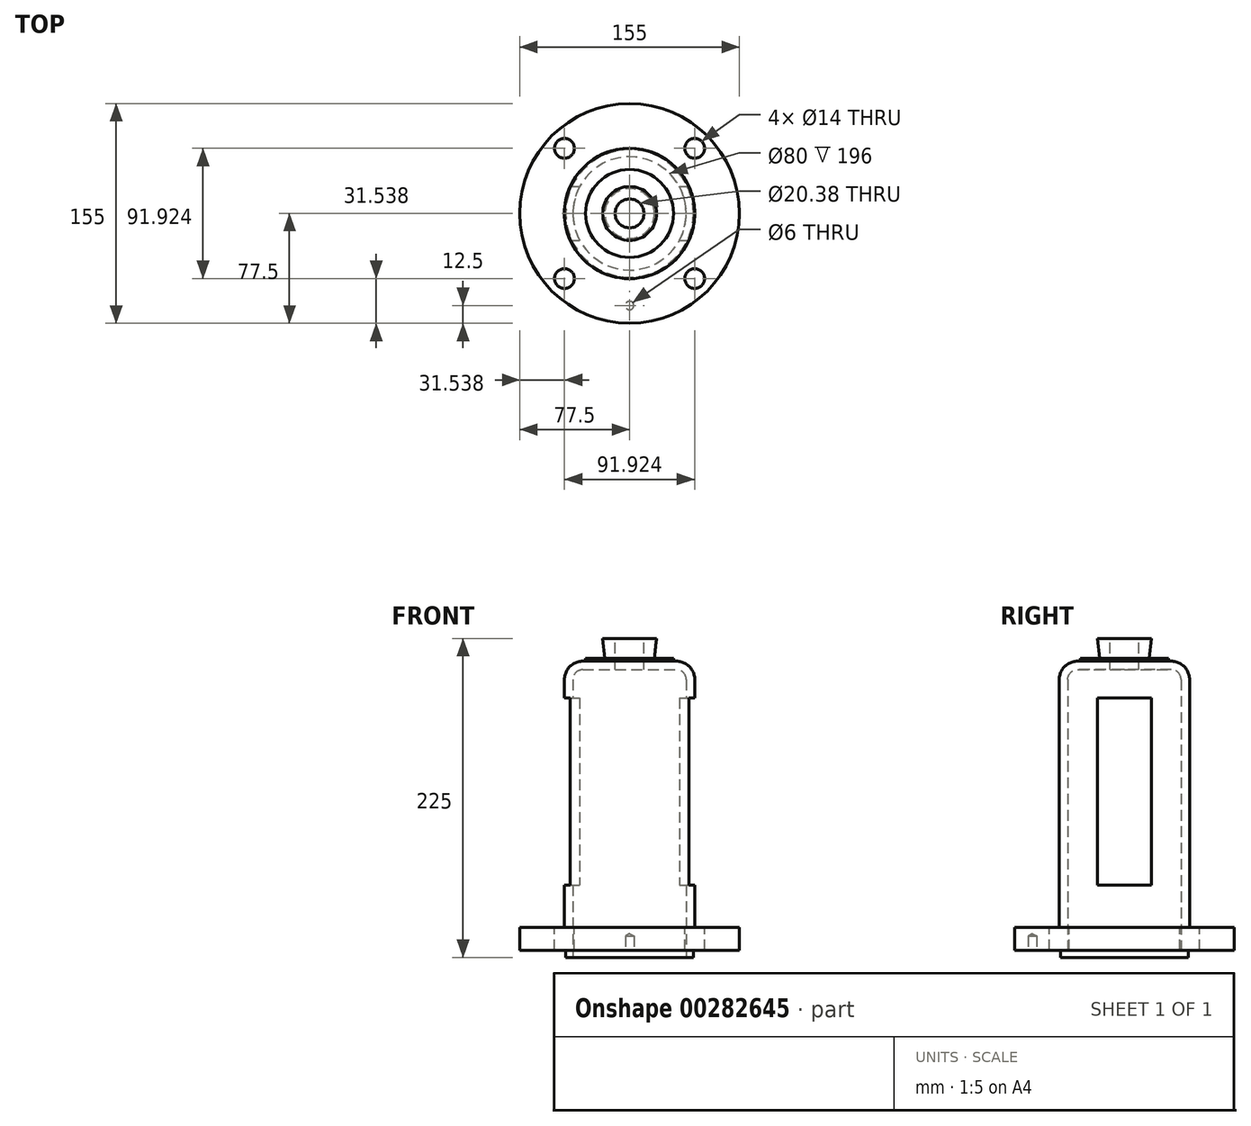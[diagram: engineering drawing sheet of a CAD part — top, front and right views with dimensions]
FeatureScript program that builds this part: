
annotation { "Feature Type Name" : "Feature", "Feature Type Description" : "" }
export const myFeature = defineFeature(function(context is Context, id is Id, definition is map)
    precondition{}
    {
        {
            var Q0;
            Q0=qCreatedBy(makeId("Right.planeOp"),FACE);
            var sketch = newSketch(context, id + "F0", { "sketchPlane" : qUnion([Q0])});
            skLineSegment(sketch, "E0", {"start": v(0, 225) * mm, "end": v(19, 225) * mm});
            skLineSegment(sketch, "E1", {"start": v(19, 225) * mm, "end": v(17.5, 211) * mm});
            skLineSegment(sketch, "E2", {"start": v(17.5, 211) * mm, "end": v(31, 211) * mm});
            skLineSegment(sketch, "E3", {"start": v(31, 211) * mm, "end": v(31, 209) * mm});
            skLineSegment(sketch, "E4", {"start": v(31, 209) * mm, "end": v(33, 209) * mm});
            skLineSegment(sketch, "E5", {"start": v(46, 196) * mm, "end": v(46, 21) * mm});
            skLineSegment(sketch, "E6", {"start": v(46, 21) * mm, "end": v(77.5, 21) * mm});
            skLineSegment(sketch, "E7", {"start": v(77.5, 21) * mm, "end": v(77.5, 5) * mm});
            skLineSegment(sketch, "E8", {"start": v(77.5, 5) * mm, "end": v(45, 5) * mm});
            skLineSegment(sketch, "E9", {"start": v(45, 5) * mm, "end": v(45, 0) * mm});
            skLineSegment(sketch, "E10", {"start": v(45, 0) * mm, "end": v(0, 0) * mm});
            skLineSegment(sketch, "E11", {"start": v(0, 0) * mm, "end": v(0, 225) * mm});
            skLineSegment(sketch, "E12", {"start": v(0, 237.35) * mm, "end": v(0, -29.5) * mm, "construction": true});
            skPoint(sketch, "E13.visualSharp", {"position": v(46, 209) * mm});
            skArc(sketch, "E13.filletArc", {"start": v(46, 196) * mm, "mid": v(42.2, 205.2) * mm, "end": v(33, 209) * mm});
            skSolve(sketch);
        }
        {
            var Q0;
            Q0=makeQuery(id+"F0.imprint","IMPRINT",FACE,{"disambiguationData":[TD([[makeQuery(id+"F0.imprint","IMPRINT",EDGE,{"derivedFrom":sQuery(id+"F0.wireOp",EDGE,"E0")}),-1.0]])]});
            var Q1;
            Q1=sQuery(id+"F0.wireOp",EDGE,"E12");
            revolve(context, id + "F1", {"entities" : qUnion([Q0]), "axis" : qUnion([Q1]), "revolveType" : RevolveType.FULL});
        }
        {
            var Q0;
            Q0=qCreatedBy(makeId("Right.planeOp"),FACE);
            var sketch = newSketch(context, id + "F2", { "sketchPlane" : qUnion([Q0])});
            skLineSegment(sketch, "E14", {"start": v(0, 203) * mm, "end": v(33, 203) * mm});
            skLineSegment(sketch, "E15", {"start": v(40, 196) * mm, "end": v(40, -6) * mm});
            skLineSegment(sketch, "E16", {"start": v(40, -6) * mm, "end": v(0, -6) * mm});
            skLineSegment(sketch, "E17", {"start": v(0, -6) * mm, "end": v(0, 203) * mm});
            skPoint(sketch, "E18.visualSharp", {"position": v(40, 203) * mm});
            skArc(sketch, "E18.filletArc", {"start": v(40, 196) * mm, "mid": v(37.95, 200.95) * mm, "end": v(33, 203) * mm});
            skSolve(sketch);
        }
        {
            var Q0;
            Q0=makeQuery(id+"F2.imprint","IMPRINT",FACE,{"disambiguationData":[TD([[makeQuery(id+"F2.imprint","IMPRINT",EDGE,{"derivedFrom":sQuery(id+"F2.wireOp",EDGE,"E14")}),-1.0]])]});
            var Q1;
            Q1=sQuery(id+"F0.wireOp",EDGE,"E12");
            revolve(context, id + "F3", {"operationType" : NewBodyOperationType.REMOVE, "entities" : qUnion([Q0]), "axis" : qUnion([Q1]), "revolveType" : RevolveType.FULL, "oppositeDirection" : true});
        }
        {
            var Q0;
            Q0=makeQuery(id+"F1.opRevolve","SWEPT_FACE",FACE,{"disambiguationData":[OSD([sQuery(id+"F0.wireOp",EDGE,"E0")])]});
            var sketch = newSketch(context, id + "F4", { "sketchPlane" : qUnion([Q0])});
            skPoint(sketch, "E19", {"position": v(0, 0) * mm});
            skSolve(sketch);
        }
        {
            var Q0;
            Q0=sQuery(id+"F4.wireOp",VERTEX,"E19");
            var Q1;
            Q1=makeQuery(id+"F1.opRevolve","SWEPT_BODY",BODY,{"disambiguationData":[OSD([sQuery(id+"F0.wireOp",EDGE,"E0"),sQuery(id+"F0.wireOp",EDGE,"E1"),sQuery(id+"F0.wireOp",EDGE,"E2"),sQuery(id+"F0.wireOp",EDGE,"E3"),sQuery(id+"F0.wireOp",EDGE,"E4"),sQuery(id+"F0.wireOp",EDGE,"E5"),sQuery(id+"F0.wireOp",EDGE,"E6"),sQuery(id+"F0.wireOp",EDGE,"E7"),sQuery(id+"F0.wireOp",EDGE,"E8"),sQuery(id+"F0.wireOp",EDGE,"E9"),sQuery(id+"F0.wireOp",EDGE,"E10"),sQuery(id+"F0.wireOp",EDGE,"E11"),sQuery(id+"F0.wireOp",EDGE,"E13.filletArc")])]});
            hole(context, id + "F5", {"style" : HoleStyle.SIMPLE, "endStyle" : HoleEndStyle.THROUGH, "standardTappedOrClearance" : lookupTablePath({ "standard" : "Custom", "fit" : "Normal", "size" : "M5", "type" : "Clearance" }), "standardBlindInLast" : lookupTablePath({ "fit" : "Standard", "standard" : "Custom", "size" : "M5", "type" : "Clearance" }), "holeDiameter" : 20.38 * mm, "tappedDepth" : 12 * mm, "tapClearance" : 3, "locations" : qUnion([Q0]), "scope" : qUnion([Q1])});
        }
        {
            var Q0;
            Q0=makeQuery(id+"F1.opRevolve","SWEPT_FACE",FACE,{"disambiguationData":[OSD([sQuery(id+"F0.wireOp",EDGE,"E6")])]});
            var sketch = newSketch(context, id + "F6", { "sketchPlane" : qUnion([Q0])});
            skLineSegment(sketch, "E20", {"start": v(0, 0) * mm, "end": v(45.96, 45.96) * mm, "construction": true});
            skLineSegment(sketch, "E21.MirrorCS", {"start": v(0, 0) * mm, "end": v(-45.96, 45.96) * mm, "construction": true});
            skLineSegment(sketch, "E22.MirrorCS", {"start": v(0, 0) * mm, "end": v(45.96, -45.96) * mm, "construction": true});
            skLineSegment(sketch, "E23.MirrorCS", {"start": v(0, 0) * mm, "end": v(-45.96, -45.96) * mm, "construction": true});
            skSolve(sketch);
        }
        {
            var Q0;
            Q0=sQuery(id+"F6.wireOp",VERTEX,"E20.end");
            var Q1;
            Q1=sQuery(id+"F6.wireOp",VERTEX,"E22.MirrorCS.end");
            var Q2;
            Q2=sQuery(id+"F6.wireOp",VERTEX,"E21.MirrorCS.end");
            var Q3;
            Q3=sQuery(id+"F6.wireOp",VERTEX,"E23.MirrorCS.end");
            var Q4;
            Q4=makeQuery(id+"F1.opRevolve","SWEPT_BODY",BODY,{"disambiguationData":[OSD([sQuery(id+"F0.wireOp",EDGE,"E0"),sQuery(id+"F0.wireOp",EDGE,"E1"),sQuery(id+"F0.wireOp",EDGE,"E2"),sQuery(id+"F0.wireOp",EDGE,"E3"),sQuery(id+"F0.wireOp",EDGE,"E4"),sQuery(id+"F0.wireOp",EDGE,"E5"),sQuery(id+"F0.wireOp",EDGE,"E6"),sQuery(id+"F0.wireOp",EDGE,"E7"),sQuery(id+"F0.wireOp",EDGE,"E8"),sQuery(id+"F0.wireOp",EDGE,"E9"),sQuery(id+"F0.wireOp",EDGE,"E10"),sQuery(id+"F0.wireOp",EDGE,"E11"),sQuery(id+"F0.wireOp",EDGE,"E13.filletArc")])]});
            hole(context, id + "F7", {"style" : HoleStyle.SIMPLE, "endStyle" : HoleEndStyle.THROUGH, "holeDiameter" : 14 * mm, "tappedDepth" : 12 * mm, "tapClearance" : 3, "locations" : qUnion([Q0, Q1, Q2, Q3]), "scope" : qUnion([Q4])});
        }
        {
            var Q0;
            Q0=qCreatedBy(makeId("Right.planeOp"),FACE);
            var sketch = newSketch(context, id + "F8", { "sketchPlane" : qUnion([Q0])});
            skLineSegment(sketch, "E24.bottom", {"start": v(-19, 183) * mm, "end": v(19, 183) * mm});
            skLineSegment(sketch, "E24.top", {"start": v(-19, 51) * mm, "end": v(19, 51) * mm});
            skLineSegment(sketch, "E24.left", {"start": v(-19, 183) * mm, "end": v(-19, 51) * mm});
            skLineSegment(sketch, "E24.right", {"start": v(19, 183) * mm, "end": v(19, 51) * mm});
            skSolve(sketch);
        }
        {
            var Q0;
            Q0 = qSketchRegion(id + "F8", true);
            extrude(context, id + "F9", {"entities" : qUnion([Q0]), "operationType" : NewBodyOperationType.REMOVE, "endBound" : BoundingType.THROUGH_ALL, "oppositeDirection" : true, "depth" : 25 * mm, "hasSecondDirection" : true, "secondDirectionBound" : SecondDirectionBoundingType.THROUGH_ALL, "secondDirectionOppositeDirection" : false, "secondDirectionDepth" : 25 * mm});
        }
        {
            var Q0;
            Q0=makeQuery(id+"F1.opRevolve","SWEPT_FACE",FACE,{"disambiguationData":[OSD([sQuery(id+"F0.wireOp",EDGE,"E8")])]});
            var sketch = newSketch(context, id + "F10", { "sketchPlane" : qUnion([Q0])});
            skPoint(sketch, "E25", {"position": v(0, 65) * mm});
            skSolve(sketch);
        }
        {
            var Q0;
            Q0=sQuery(id+"F10.wireOp",VERTEX,"E25");
            var Q1;
            Q1=makeQuery(id+"F1.opRevolve","SWEPT_BODY",BODY,{"disambiguationData":[OSD([sQuery(id+"F0.wireOp",EDGE,"E0"),sQuery(id+"F0.wireOp",EDGE,"E1"),sQuery(id+"F0.wireOp",EDGE,"E2"),sQuery(id+"F0.wireOp",EDGE,"E3"),sQuery(id+"F0.wireOp",EDGE,"E4"),sQuery(id+"F0.wireOp",EDGE,"E5"),sQuery(id+"F0.wireOp",EDGE,"E6"),sQuery(id+"F0.wireOp",EDGE,"E7"),sQuery(id+"F0.wireOp",EDGE,"E8"),sQuery(id+"F0.wireOp",EDGE,"E9"),sQuery(id+"F0.wireOp",EDGE,"E10"),sQuery(id+"F0.wireOp",EDGE,"E11"),sQuery(id+"F0.wireOp",EDGE,"E13.filletArc")])]});
            hole(context, id + "F11", {"style" : HoleStyle.SIMPLE, "endStyle" : HoleEndStyle.BLIND, "holeDiameter" : 6 * mm, "holeDepth" : 10 * mm, "tappedDepth" : 12 * mm, "tapClearance" : 3, "locations" : qUnion([Q0]), "scope" : qUnion([Q1])});
        }
    });
